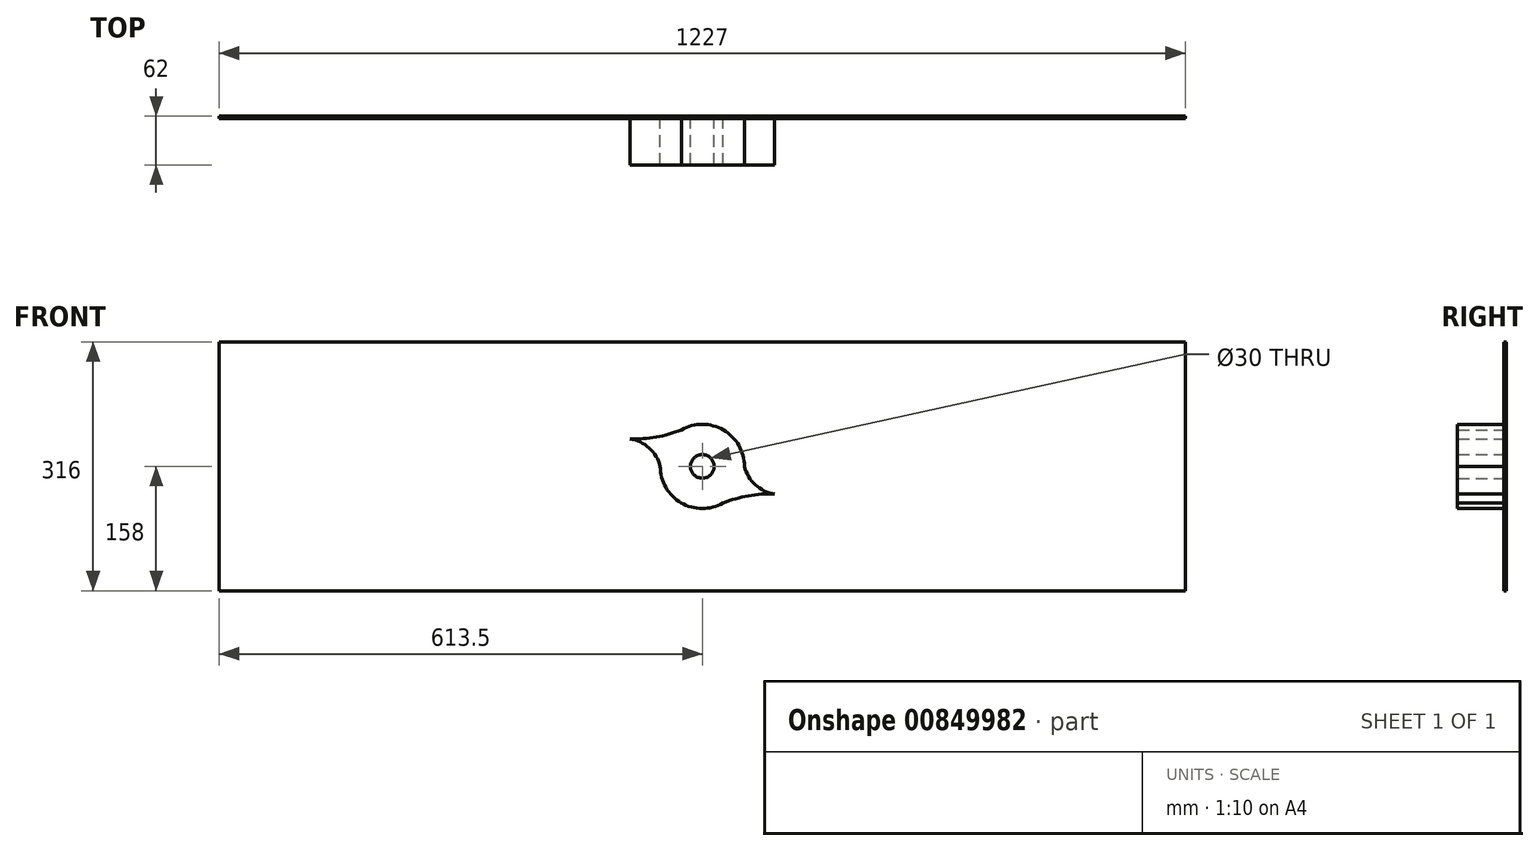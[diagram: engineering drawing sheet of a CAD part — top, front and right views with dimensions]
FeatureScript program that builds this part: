
annotation { "Feature Type Name" : "Feature", "Feature Type Description" : "" }
export const myFeature = defineFeature(function(context is Context, id is Id, definition is map)
    precondition{}
    {
        {
            var Q0;
            Q0=qCreatedBy(makeId("Front.planeOp"),FACE);
            var sketch = newSketch(context, id + "F0", { "sketchPlane" : qUnion([Q0])});
            skArc(sketch, "E0", {"start": v(0, -15) * mm, "mid": v(15, 0) * mm, "end": v(0, 15) * mm});
            skArc(sketch, "E1", {"start": v(0, 15) * mm, "mid": v(-15, 0) * mm, "end": v(0, -15) * mm});
            skArc(sketch, "E2", {"start": v(0, -46) * mm, "mid": v(46, 0) * mm, "end": v(0, 46) * mm});
            skArc(sketch, "E3", {"start": v(0, 46) * mm, "mid": v(-46, 0) * mm, "end": v(0, -46) * mm});
            skArc(sketch, "E4", {"start": v(-53.5, 0) * mm, "mid": v(-26.87, -46.26) * mm, "end": v(26.5, -46.48) * mm});
            skArc(sketch, "E5", {"start": v(-92, 35) * mm, "mid": v(-58.65, 37.3) * mm, "end": v(-26.5, 46.48) * mm});
            skArc(sketch, "E6", {"start": v(-53.5, 0) * mm, "mid": v(-67.4, 23.39) * mm, "end": v(-92, 35) * mm});
            skArc(sketch, "E7", {"start": v(53.5, 0) * mm, "mid": v(67.4, -23.39) * mm, "end": v(92, -35) * mm});
            skArc(sketch, "E8", {"start": v(92, -35) * mm, "mid": v(58.65, -37.3) * mm, "end": v(26.5, -46.48) * mm});
            skArc(sketch, "E9.trimOffspring", {"start": v(53.5, 0) * mm, "mid": v(26.87, 46.26) * mm, "end": v(-26.5, 46.48) * mm});
            skPoint(sketch, "E10", {"position": v(0, 53.5) * mm});
            skPoint(sketch, "E11", {"position": v(0, -53.5) * mm});
            skSolve(sketch);
        }
        {
            var Q0;
            Q0=qCreatedBy(makeId("Front.planeOp"),FACE);
            var sketch = newSketch(context, id + "F1", { "sketchPlane" : qUnion([Q0])});
            skLineSegment(sketch, "E12.bottom", {"start": v(613.5, 158) * mm, "end": v(-613.5, 158) * mm});
            skLineSegment(sketch, "E12.top", {"start": v(613.5, -158) * mm, "end": v(-613.5, -158) * mm});
            skLineSegment(sketch, "E12.left", {"start": v(613.5, 158) * mm, "end": v(613.5, -158) * mm});
            skLineSegment(sketch, "E12.right", {"start": v(-613.5, 158) * mm, "end": v(-613.5, -158) * mm});
            skPoint(sketch, "E12.middle", {"position": v(0, 0) * mm});
            skSolve(sketch);
        }
        {
            var Q0;
            Q0=makeQuery(id+"F1.imprint","IMPRINT",FACE,{"disambiguationData":[TD([[makeQuery(id+"F1.imprint","IMPRINT",EDGE,{"derivedFrom":sQuery(id+"F1.wireOp",EDGE,"E12.bottom")}),1.0]])]});
            cPlane(context, id + "F2", {"entities" : qUnion([Q0]), "cplaneType" : CPlaneType.OFFSET, "offset" : 62 * mm, "width" : 150 * mm, "height" : 150 * mm});
        }
        {
            var Q0;
            Q0 = qSketchRegion(id + "F0", true);
            var Q1;
            Q1=makeQuery(id+"F0.imprint","IMPRINT",FACE,{"disambiguationData":[TD([[makeQuery(id+"F0.imprint","IMPRINT",EDGE,{"derivedFrom":sQuery(id+"F0.wireOp",EDGE,"E0")}),-1.0]])]});
            var Q2;
            Q2=qCreatedBy(id+"F2.planeOp",FACE);
            extrude(context, id + "F3", {"entities" : qUnion([Q0, Q1]), "endBound" : BoundingType.UP_TO_SURFACE, "depth" : 25 * mm, "endBoundEntityFace" : qUnion([Q2]), "offsetDistance" : 25 * mm});
        }
        {
            var Q0;
            Q0 = qSketchRegion(id + "F1", true);
            extrude(context, id + "F4", {"entities" : qUnion([Q0]), "depth" : 3.1 * mm, "offsetDistance" : 25 * mm});
        }
    });
